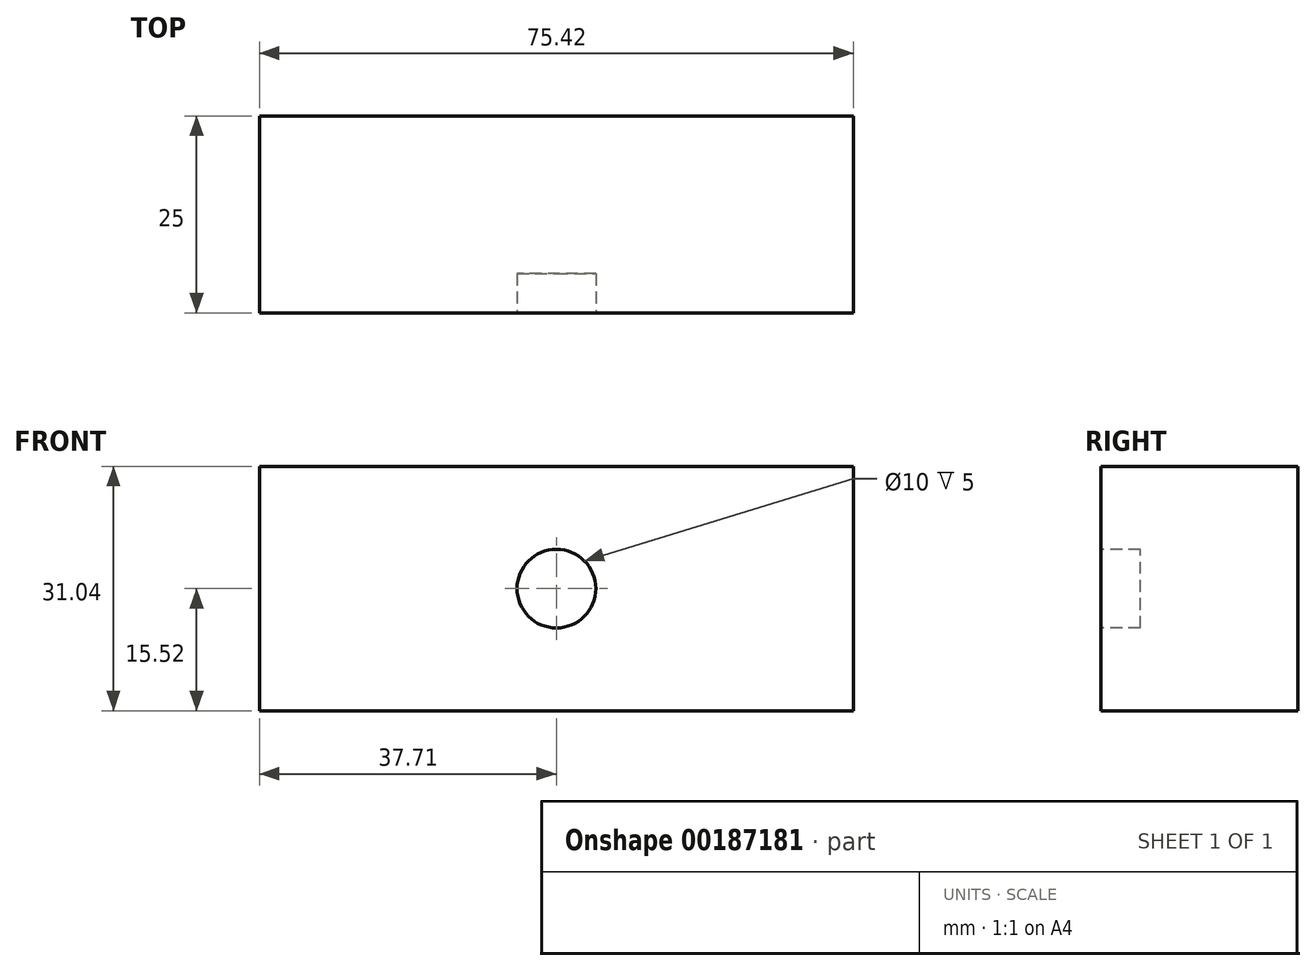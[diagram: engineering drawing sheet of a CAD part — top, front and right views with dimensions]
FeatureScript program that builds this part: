
annotation { "Feature Type Name" : "Feature", "Feature Type Description" : "" }
export const myFeature = defineFeature(function(context is Context, id is Id, definition is map)
    precondition{}
    {
        {
            var Q0;
            Q0=qCreatedBy(makeId("Front.planeOp"),FACE);
            var sketch = newSketch(context, id + "F0", { "sketchPlane" : qUnion([Q0])});
            skLineSegment(sketch, "E0.bottom", {"start": v(-37.7, 15.52) * mm, "end": v(37.7, 15.52) * mm});
            skLineSegment(sketch, "E0.top", {"start": v(-37.7, -15.52) * mm, "end": v(37.7, -15.52) * mm});
            skLineSegment(sketch, "E0.left", {"start": v(-37.7, 15.52) * mm, "end": v(-37.7, -15.52) * mm});
            skLineSegment(sketch, "E0.right", {"start": v(37.7, 15.52) * mm, "end": v(37.7, -15.52) * mm});
            skPoint(sketch, "E0.middle", {"position": v(0, 0) * mm});
            skSolve(sketch);
        }
        {
            var Q0;
            Q0 = qSketchRegion(id + "F0", true);
            extrude(context, id + "F1", {"entities" : qUnion([Q0]), "depth" : 25 * mm});
        }
        {
            var Q0;
            Q0=makeQuery(id+"F1.opExtrude","CAP_FACE",FACE,{"disambiguationData":[OSD([sQuery(id+"F0.wireOp",EDGE,"E0.bottom"),sQuery(id+"F0.wireOp",EDGE,"E0.top"),sQuery(id+"F0.wireOp",EDGE,"E0.left"),sQuery(id+"F0.wireOp",EDGE,"E0.right")])],"isStart":false});
            var sketch = newSketch(context, id + "F2", { "sketchPlane" : qUnion([Q0])});
            skCircle(sketch, "E1", {"center": v(0, 0) * mm, "radius": 5 * mm});
            skSolve(sketch);
        }
        {
            var Q0;
            Q0 = qSketchRegion(id + "F2", true);
            extrude(context, id + "F3", {"entities" : qUnion([Q0]), "operationType" : NewBodyOperationType.REMOVE, "oppositeDirection" : true, "depth" : 5 * mm});
        }
    });
